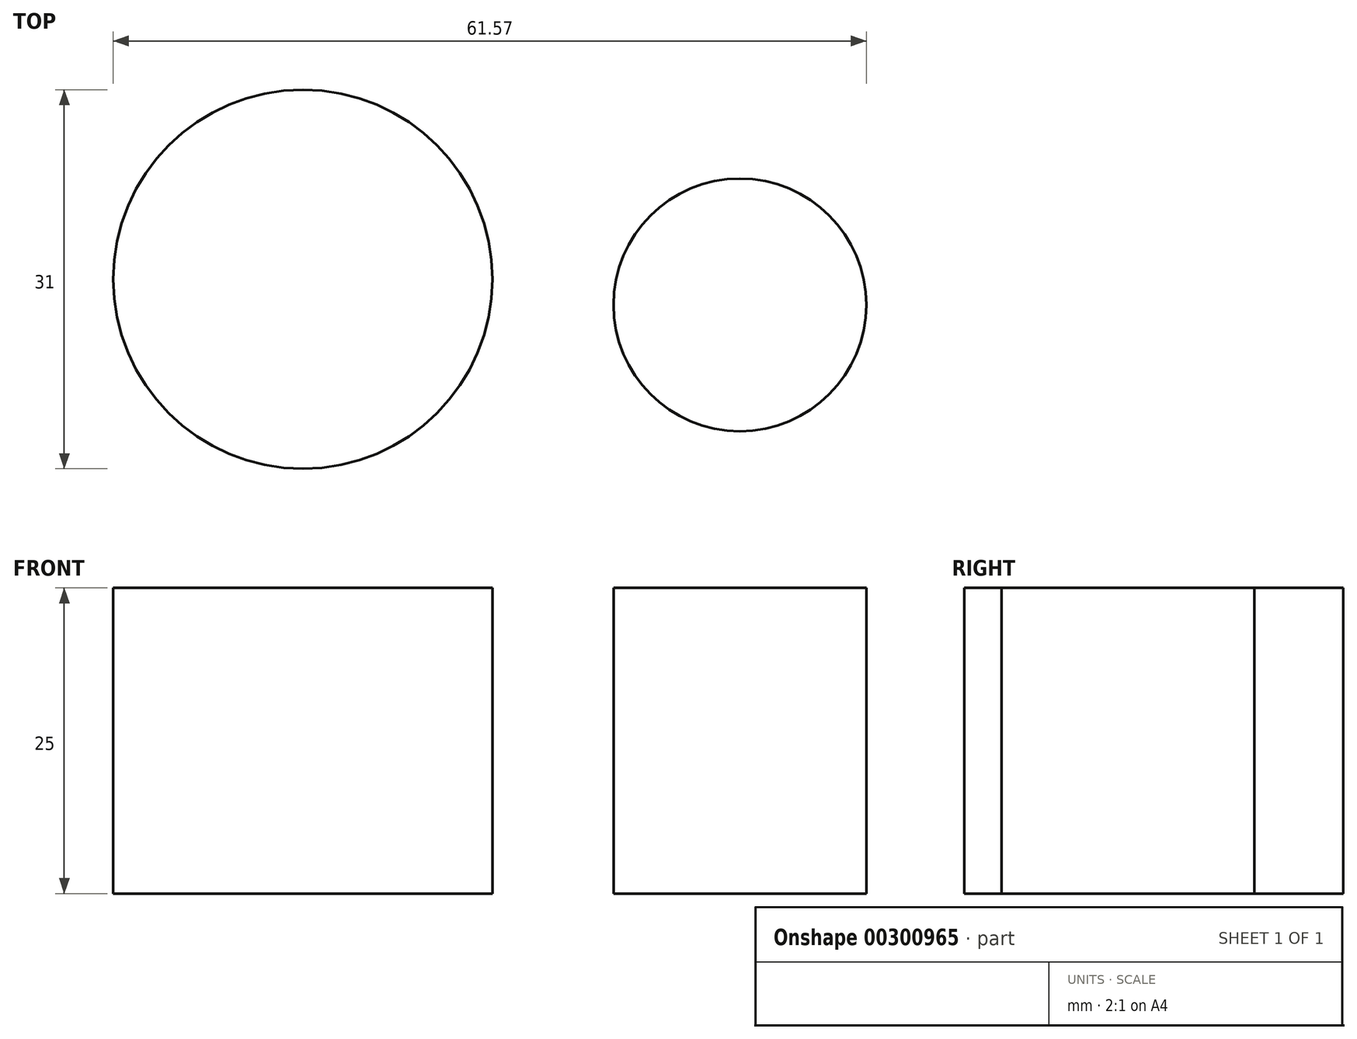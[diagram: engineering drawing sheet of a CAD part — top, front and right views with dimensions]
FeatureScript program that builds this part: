
annotation { "Feature Type Name" : "Feature", "Feature Type Description" : "" }
export const myFeature = defineFeature(function(context is Context, id is Id, definition is map)
    precondition{}
    {
        {
            var Q0;
            Q0=qCreatedBy(makeId("Top.planeOp"),FACE);
            var sketch = newSketch(context, id + "F0", { "sketchPlane" : qUnion([Q0])});
            skCircle(sketch, "E0", {"center": v(-52.5, 42.45) * mm, "radius": 15.5 * mm});
            skCircle(sketch, "E1", {"center": v(-16.77, 40.35) * mm, "radius": 10.33 * mm});
            skSolve(sketch);
        }
        {
            var Q0;
            Q0 = qSketchRegion(id + "F0", true);
            extrude(context, id + "F1", {"entities" : qUnion([Q0]), "depth" : 25 * mm});
        }
    });
